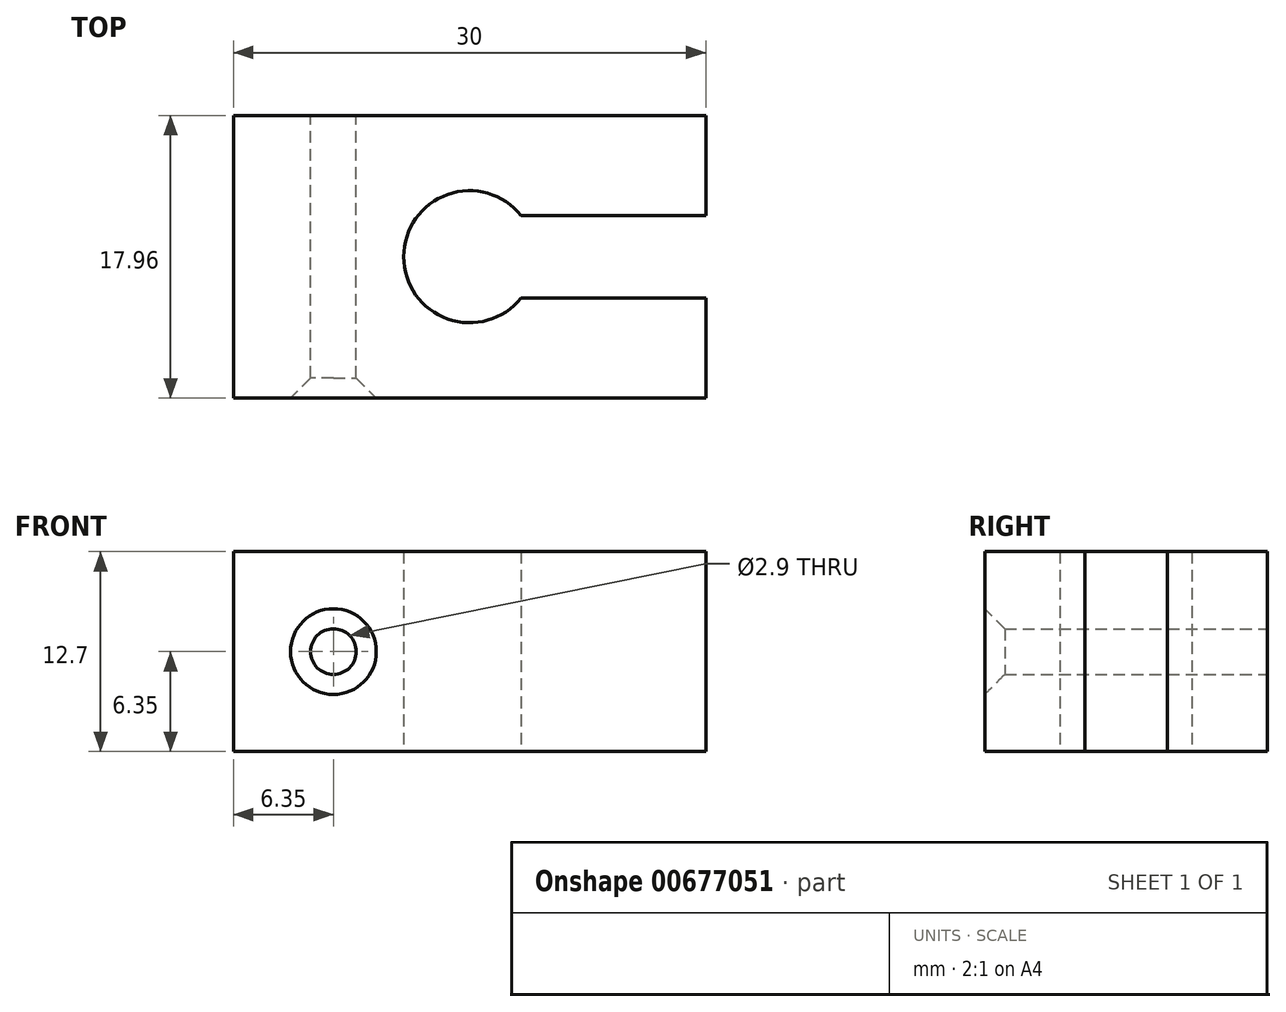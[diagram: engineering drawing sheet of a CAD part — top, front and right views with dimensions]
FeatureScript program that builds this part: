
annotation { "Feature Type Name" : "Feature", "Feature Type Description" : "" }
export const myFeature = defineFeature(function(context is Context, id is Id, definition is map)
    precondition{}
    {
        {
            var Q0;
            Q0=qCreatedBy(makeId("Top.planeOp"),FACE);
            var sketch = newSketch(context, id + "F0", { "sketchPlane" : qUnion([Q0])});
            skLineSegment(sketch, "E0.bottom", {"start": v(15, 8.98) * mm, "end": v(-15, 8.98) * mm});
            skLineSegment(sketch, "E0.top", {"start": v(15, -8.98) * mm, "end": v(-15, -8.98) * mm});
            skLineSegment(sketch, "E0.left", {"start": v(15, 8.98) * mm, "end": v(15, -8.98) * mm});
            skLineSegment(sketch, "E0.right", {"start": v(-15, 8.98) * mm, "end": v(-15, -8.98) * mm});
            skPoint(sketch, "E0.middle", {"position": v(0, 0) * mm});
            skLineSegment(sketch, "E1", {"start": v(15, 2.63) * mm, "end": v(0, 2.62) * mm});
            skLineSegment(sketch, "E2", {"start": v(0, 2.62) * mm, "end": v(0, -2.63) * mm});
            skLineSegment(sketch, "E3", {"start": v(0, -2.63) * mm, "end": v(15, -2.63) * mm});
            skCircle(sketch, "E4", {"center": v(0, 0) * mm, "radius": 4.2 * mm});
            skSolve(sketch);
        }
        {
            var Q0;
            {var subQ4=sQuery(id+"F0.wireOp",EDGE,"E0.bottom");Q0=makeQuery(id+"F0.imprint","IMPRINT",FACE,{"disambiguationData":[TD([[makeQuery(id+"F0.imprint","IMPRINT",EDGE,{"derivedFrom":subQ4}),1.0]])]});}
            extrude(context, id + "F1", {"entities" : qUnion([Q0]), "depth" : 12.7 * mm, "offsetDistance" : 25.4 * mm});
        }
        {
            var Q0;
            Q0=makeQuery(id+"F1.opExtrude","SWEPT_FACE",FACE,{"disambiguationData":[OSD([sQuery(id+"F0.wireOp",EDGE,"E0.bottom")])]});
            var sketch = newSketch(context, id + "F2", { "sketchPlane" : qUnion([Q0])});
            skCircle(sketch, "E5", {"center": v(8.65, 6.35) * mm, "radius": 1.45 * mm});
            skPoint(sketch, "E5.centerSnap0", {"position": v(15, 6.35) * mm});
            skSolve(sketch);
        }
        {
            var Q0;
            Q0=makeQuery(id+"F2.imprint","IMPRINT",FACE,{"disambiguationData":[TD([[makeQuery(id+"F2.imprint","IMPRINT",EDGE,{"derivedFrom":sQuery(id+"F2.wireOp",EDGE,"E5")}),1.0]])]});
            extrude(context, id + "F3", {"entities" : qUnion([Q0]), "operationType" : NewBodyOperationType.REMOVE, "oppositeDirection" : true, "depth" : 29.29 * mm, "offsetDistance" : 25.4 * mm});
        }
        {
            var Q0;
            Q0=makeQuery(id+"F3.boolean.opBoolean","COPY",EDGE,{"derivedFrom":makeQuery(id+"F3.opExtrude","CAP_EDGE",EDGE,{"disambiguationData":[OSD([sQuery(id+"F2.wireOp",EDGE,"E5")])],"isStart":true})});
            var Q1;
            Q1=makeQuery(id+"F3.boolean.opBoolean","INTERSECT",EDGE,{"derivedFrom":[makeQuery(id+"F1.opExtrude","SWEPT_FACE",FACE,{"disambiguationData":[OSD([sQuery(id+"F0.wireOp",EDGE,"E0.top")])]}),makeQuery(id+"F3.opExtrude","SWEPT_FACE",FACE,{"disambiguationData":[OSD([sQuery(id+"F2.wireOp",EDGE,"E5")])]})]});
            chamfer(context, id + "F4", {"entities" : qUnion([Q0, Q1]), "width" : 1.27 * mm, "tangentPropagation" : true});
        }
    });
